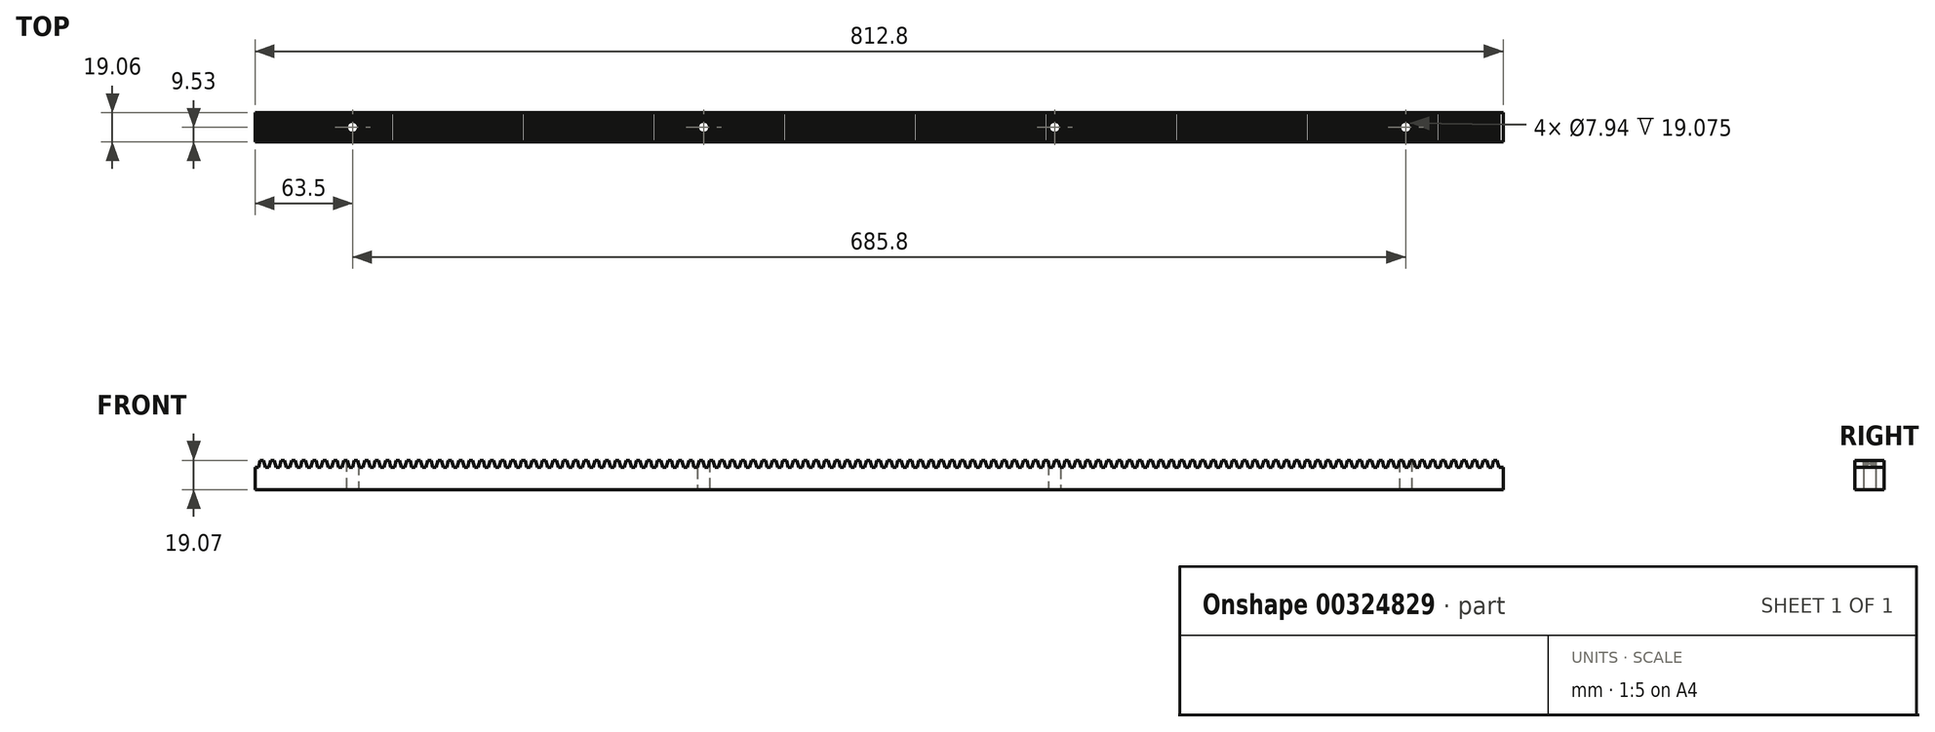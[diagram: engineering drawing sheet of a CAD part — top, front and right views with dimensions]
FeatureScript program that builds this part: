
annotation { "Feature Type Name" : "Feature", "Feature Type Description" : "" }
export const myFeature = defineFeature(function(context is Context, id is Id, definition is map)
    precondition{}
    {
        {
            var Q0;
            Q0=qCreatedBy(makeId("Right.planeOp"),FACE);
            var sketch = newSketch(context, id + "F0", { "sketchPlane" : qUnion([Q0])});
            skLineSegment(sketch, "E0.bottom", {"start": v(-9.52, 7.25) * mm, "end": v(9.53, 7.25) * mm});
            skLineSegment(sketch, "E0.top", {"start": v(-9.53, -7.25) * mm, "end": v(9.52, -7.25) * mm});
            skLineSegment(sketch, "E0.left", {"start": v(-9.52, 7.25) * mm, "end": v(-9.53, -7.25) * mm});
            skLineSegment(sketch, "E0.right", {"start": v(9.53, 7.25) * mm, "end": v(9.52, -7.25) * mm});
            skPoint(sketch, "E0.middle", {"position": v(0, 0) * mm});
            skSolve(sketch);
        }
        {
            var Q0;
            Q0=qSketchRegion(id+"F0",true);
            extrude(context, id + "F1", {"entities" : qUnion([Q0]), "endBound" : BoundingType.SYMMETRIC, "depth" : 812.8 * mm});
        }
        {
            var Q0;
            Q0=makeQuery(id+"F1.opExtrude","SWEPT_FACE",FACE,{"disambiguationData":[OSD([sQuery(id+"F0.wireOp",EDGE,"E0.left")])]});
            var sketch = newSketch(context, id + "F2", { "sketchPlane" : qUnion([Q0])});
            skLineSegment(sketch, "E1.0", {"start": v(406.4, 7.25) * mm, "end": v(-406.4, 7.25) * mm});
            skLineSegment(sketch, "E2.0", {"start": v(406.4, 11.82) * mm, "end": v(-406.4, 11.82) * mm, "construction": true});
            skLineSegment(sketch, "E3", {"start": v(-406.4, 7.25) * mm, "end": v(-406.4, 19.13) * mm, "construction": true});
            skLineSegment(sketch, "E4.0", {"start": v(-404.16, 7.25) * mm, "end": v(-404.16, 19.13) * mm, "construction": true});
            skLineSegment(sketch, "E5.0", {"start": v(-403, 7.25) * mm, "end": v(-403, 19.13) * mm, "construction": true});
            skLineSegment(sketch, "E6.0", {"start": v(-400.76, 7.25) * mm, "end": v(-400.76, 19.13) * mm, "construction": true});
            skLineSegment(sketch, "E7.0", {"start": v(-399.6, 7.25) * mm, "end": v(-399.6, 19.13) * mm, "construction": true});
            skLineSegment(sketch, "E8", {"start": v(-406.4, 7.25) * mm, "end": v(-404.16, 7.25) * mm});
            skLineSegment(sketch, "E9", {"start": v(-403, 11.82) * mm, "end": v(-404.16, 7.25) * mm});
            skLineSegment(sketch, "E10", {"start": v(-403, 11.82) * mm, "end": v(-400.76, 11.82) * mm});
            skLineSegment(sketch, "E11", {"start": v(-400.76, 11.82) * mm, "end": v(-399.6, 7.25) * mm});
            skLineSegment(sketch, "E12.1.0.0", {"start": v(-399.6, 7.25) * mm, "end": v(-397.36, 7.25) * mm});
            skLineSegment(sketch, "E12.1.0.1", {"start": v(-393.95, 11.82) * mm, "end": v(-392.79, 7.25) * mm});
            skLineSegment(sketch, "E12.1.0.2", {"start": v(-396.19, 11.82) * mm, "end": v(-393.95, 11.82) * mm});
            skLineSegment(sketch, "E12.1.0.3", {"start": v(-396.19, 11.82) * mm, "end": v(-397.36, 7.25) * mm});
            skLineSegment(sketch, "E12.2.0.0", {"start": v(-392.79, 7.25) * mm, "end": v(-390.55, 7.25) * mm});
            skLineSegment(sketch, "E12.2.0.1", {"start": v(-387.15, 11.82) * mm, "end": v(-385.98, 7.25) * mm});
            skLineSegment(sketch, "E12.2.0.2", {"start": v(-389.38, 11.82) * mm, "end": v(-387.15, 11.82) * mm});
            skLineSegment(sketch, "E12.2.0.3", {"start": v(-389.38, 11.82) * mm, "end": v(-390.55, 7.25) * mm});
            skLineSegment(sketch, "E12.3.0.0", {"start": v(-385.98, 7.25) * mm, "end": v(-383.74, 7.25) * mm});
            skLineSegment(sketch, "E12.3.0.1", {"start": v(-380.34, 11.82) * mm, "end": v(-379.17, 7.25) * mm});
            skLineSegment(sketch, "E12.3.0.2", {"start": v(-382.57, 11.82) * mm, "end": v(-380.34, 11.82) * mm});
            skLineSegment(sketch, "E12.3.0.3", {"start": v(-382.57, 11.82) * mm, "end": v(-383.74, 7.25) * mm});
            skLineSegment(sketch, "E12.4.0.0", {"start": v(-379.17, 7.25) * mm, "end": v(-376.94, 7.25) * mm});
            skLineSegment(sketch, "E12.4.0.1", {"start": v(-373.53, 11.82) * mm, "end": v(-372.36, 7.25) * mm});
            skLineSegment(sketch, "E12.4.0.2", {"start": v(-375.77, 11.82) * mm, "end": v(-373.53, 11.82) * mm});
            skLineSegment(sketch, "E12.4.0.3", {"start": v(-375.77, 11.82) * mm, "end": v(-376.94, 7.25) * mm});
            skLineSegment(sketch, "E12.5.0.0", {"start": v(-372.36, 7.25) * mm, "end": v(-370.13, 7.25) * mm});
            skLineSegment(sketch, "E12.5.0.1", {"start": v(-366.73, 11.82) * mm, "end": v(-365.56, 7.25) * mm});
            skLineSegment(sketch, "E12.5.0.2", {"start": v(-368.96, 11.82) * mm, "end": v(-366.73, 11.82) * mm});
            skLineSegment(sketch, "E12.5.0.3", {"start": v(-368.96, 11.82) * mm, "end": v(-370.13, 7.25) * mm});
            skLineSegment(sketch, "E12.6.0.0", {"start": v(-365.56, 7.25) * mm, "end": v(-363.32, 7.25) * mm});
            skLineSegment(sketch, "E12.6.0.1", {"start": v(-359.92, 11.82) * mm, "end": v(-358.75, 7.25) * mm});
            skLineSegment(sketch, "E12.6.0.2", {"start": v(-362.15, 11.82) * mm, "end": v(-359.92, 11.82) * mm});
            skLineSegment(sketch, "E12.6.0.3", {"start": v(-362.15, 11.82) * mm, "end": v(-363.32, 7.25) * mm});
            skLineSegment(sketch, "E12.7.0.0", {"start": v(-358.75, 7.25) * mm, "end": v(-356.51, 7.25) * mm});
            skLineSegment(sketch, "E12.7.0.1", {"start": v(-353.11, 11.82) * mm, "end": v(-351.94, 7.25) * mm});
            skLineSegment(sketch, "E12.7.0.2", {"start": v(-355.35, 11.82) * mm, "end": v(-353.11, 11.82) * mm});
            skLineSegment(sketch, "E12.7.0.3", {"start": v(-355.35, 11.82) * mm, "end": v(-356.51, 7.25) * mm});
            skLineSegment(sketch, "E12.8.0.0", {"start": v(-351.94, 7.25) * mm, "end": v(-349.7, 7.25) * mm});
            skLineSegment(sketch, "E12.8.0.1", {"start": v(-346.3, 11.82) * mm, "end": v(-345.14, 7.25) * mm});
            skLineSegment(sketch, "E12.8.0.2", {"start": v(-348.54, 11.82) * mm, "end": v(-346.3, 11.82) * mm});
            skLineSegment(sketch, "E12.8.0.3", {"start": v(-348.54, 11.82) * mm, "end": v(-349.7, 7.25) * mm});
            skLineSegment(sketch, "E12.9.0.0", {"start": v(-345.14, 7.25) * mm, "end": v(-342.9, 7.25) * mm});
            skLineSegment(sketch, "E12.9.0.1", {"start": v(-339.5, 11.82) * mm, "end": v(-338.33, 7.25) * mm});
            skLineSegment(sketch, "E12.9.0.2", {"start": v(-341.73, 11.82) * mm, "end": v(-339.5, 11.82) * mm});
            skLineSegment(sketch, "E12.9.0.3", {"start": v(-341.73, 11.82) * mm, "end": v(-342.9, 7.25) * mm});
            skLineSegment(sketch, "E12.10.0.0", {"start": v(-338.33, 7.25) * mm, "end": v(-336.1, 7.25) * mm});
            skLineSegment(sketch, "E12.10.0.1", {"start": v(-332.69, 11.82) * mm, "end": v(-331.52, 7.25) * mm});
            skLineSegment(sketch, "E12.10.0.2", {"start": v(-334.92, 11.82) * mm, "end": v(-332.69, 11.82) * mm});
            skLineSegment(sketch, "E12.10.0.3", {"start": v(-334.92, 11.82) * mm, "end": v(-336.1, 7.25) * mm});
            skLineSegment(sketch, "E12.11.0.0", {"start": v(-331.52, 7.25) * mm, "end": v(-329.29, 7.25) * mm});
            skLineSegment(sketch, "E12.11.0.1", {"start": v(-325.88, 11.82) * mm, "end": v(-324.71, 7.25) * mm});
            skLineSegment(sketch, "E12.11.0.2", {"start": v(-328.12, 11.82) * mm, "end": v(-325.88, 11.82) * mm});
            skLineSegment(sketch, "E12.11.0.3", {"start": v(-328.12, 11.82) * mm, "end": v(-329.29, 7.25) * mm});
            skLineSegment(sketch, "E12.12.0.0", {"start": v(-324.71, 7.25) * mm, "end": v(-322.48, 7.25) * mm});
            skLineSegment(sketch, "E12.12.0.1", {"start": v(-319.07, 11.82) * mm, "end": v(-317.9, 7.25) * mm});
            skLineSegment(sketch, "E12.12.0.2", {"start": v(-321.3, 11.82) * mm, "end": v(-319.07, 11.82) * mm});
            skLineSegment(sketch, "E12.12.0.3", {"start": v(-321.3, 11.82) * mm, "end": v(-322.48, 7.25) * mm});
            skLineSegment(sketch, "E12.13.0.0", {"start": v(-317.9, 7.25) * mm, "end": v(-315.67, 7.25) * mm});
            skLineSegment(sketch, "E12.13.0.1", {"start": v(-312.27, 11.82) * mm, "end": v(-311.1, 7.25) * mm});
            skLineSegment(sketch, "E12.13.0.2", {"start": v(-314.5, 11.82) * mm, "end": v(-312.27, 11.82) * mm});
            skLineSegment(sketch, "E12.13.0.3", {"start": v(-314.5, 11.82) * mm, "end": v(-315.67, 7.25) * mm});
            skLineSegment(sketch, "E12.14.0.0", {"start": v(-311.1, 7.25) * mm, "end": v(-308.86, 7.25) * mm});
            skLineSegment(sketch, "E12.14.0.1", {"start": v(-305.46, 11.82) * mm, "end": v(-304.3, 7.25) * mm});
            skLineSegment(sketch, "E12.14.0.2", {"start": v(-307.7, 11.82) * mm, "end": v(-305.46, 11.82) * mm});
            skLineSegment(sketch, "E12.14.0.3", {"start": v(-307.7, 11.82) * mm, "end": v(-308.86, 7.25) * mm});
            skLineSegment(sketch, "E12.15.0.0", {"start": v(-304.3, 7.25) * mm, "end": v(-302.06, 7.25) * mm});
            skLineSegment(sketch, "E12.15.0.1", {"start": v(-298.65, 11.82) * mm, "end": v(-297.48, 7.25) * mm});
            skLineSegment(sketch, "E12.15.0.2", {"start": v(-300.89, 11.82) * mm, "end": v(-298.65, 11.82) * mm});
            skLineSegment(sketch, "E12.15.0.3", {"start": v(-300.89, 11.82) * mm, "end": v(-302.06, 7.25) * mm});
            skLineSegment(sketch, "E12.16.0.0", {"start": v(-297.48, 7.25) * mm, "end": v(-295.25, 7.25) * mm});
            skLineSegment(sketch, "E12.16.0.1", {"start": v(-291.85, 11.82) * mm, "end": v(-290.68, 7.25) * mm});
            skLineSegment(sketch, "E12.16.0.2", {"start": v(-294.08, 11.82) * mm, "end": v(-291.85, 11.82) * mm});
            skLineSegment(sketch, "E12.16.0.3", {"start": v(-294.08, 11.82) * mm, "end": v(-295.25, 7.25) * mm});
            skLineSegment(sketch, "E12.17.0.0", {"start": v(-290.68, 7.25) * mm, "end": v(-288.44, 7.25) * mm});
            skLineSegment(sketch, "E12.17.0.1", {"start": v(-285.04, 11.82) * mm, "end": v(-283.87, 7.25) * mm});
            skLineSegment(sketch, "E12.17.0.2", {"start": v(-287.27, 11.82) * mm, "end": v(-285.04, 11.82) * mm});
            skLineSegment(sketch, "E12.17.0.3", {"start": v(-287.27, 11.82) * mm, "end": v(-288.44, 7.25) * mm});
            skLineSegment(sketch, "E12.18.0.0", {"start": v(-283.87, 7.25) * mm, "end": v(-281.64, 7.25) * mm});
            skLineSegment(sketch, "E12.18.0.1", {"start": v(-278.23, 11.82) * mm, "end": v(-277.06, 7.25) * mm});
            skLineSegment(sketch, "E12.18.0.2", {"start": v(-280.47, 11.82) * mm, "end": v(-278.23, 11.82) * mm});
            skLineSegment(sketch, "E12.18.0.3", {"start": v(-280.47, 11.82) * mm, "end": v(-281.64, 7.25) * mm});
            skLineSegment(sketch, "E12.19.0.0", {"start": v(-277.06, 7.25) * mm, "end": v(-274.83, 7.25) * mm});
            skLineSegment(sketch, "E12.19.0.1", {"start": v(-271.42, 11.82) * mm, "end": v(-270.26, 7.25) * mm});
            skLineSegment(sketch, "E12.19.0.2", {"start": v(-273.66, 11.82) * mm, "end": v(-271.42, 11.82) * mm});
            skLineSegment(sketch, "E12.19.0.3", {"start": v(-273.66, 11.82) * mm, "end": v(-274.83, 7.25) * mm});
            skLineSegment(sketch, "E12.direction1", {"start": v(-406.4, 7.25) * mm, "end": v(-399.6, 7.25) * mm, "construction": true});
            skLineSegment(sketch, "E13.1.0.0", {"start": v(-264.62, 11.82) * mm, "end": v(-263.45, 7.25) * mm});
            skLineSegment(sketch, "E13.1.0.1", {"start": v(-266.85, 11.82) * mm, "end": v(-264.62, 11.82) * mm});
            skLineSegment(sketch, "E13.1.0.2", {"start": v(-266.85, 11.82) * mm, "end": v(-268.02, 7.25) * mm});
            skLineSegment(sketch, "E13.1.0.3", {"start": v(-270.26, 7.25) * mm, "end": v(-268.02, 7.25) * mm});
            skLineSegment(sketch, "E13.2.0.0", {"start": v(-257.8, 11.82) * mm, "end": v(-256.64, 7.25) * mm});
            skLineSegment(sketch, "E13.2.0.1", {"start": v(-260.05, 11.82) * mm, "end": v(-257.8, 11.82) * mm});
            skLineSegment(sketch, "E13.2.0.2", {"start": v(-260.05, 11.82) * mm, "end": v(-261.21, 7.25) * mm});
            skLineSegment(sketch, "E13.2.0.3", {"start": v(-263.45, 7.25) * mm, "end": v(-261.21, 7.25) * mm});
            skLineSegment(sketch, "E13.3.0.0", {"start": v(-251, 11.82) * mm, "end": v(-249.83, 7.25) * mm});
            skLineSegment(sketch, "E13.3.0.1", {"start": v(-253.24, 11.82) * mm, "end": v(-251, 11.82) * mm});
            skLineSegment(sketch, "E13.3.0.2", {"start": v(-253.24, 11.82) * mm, "end": v(-254.4, 7.25) * mm});
            skLineSegment(sketch, "E13.3.0.3", {"start": v(-256.64, 7.25) * mm, "end": v(-254.4, 7.25) * mm});
            skLineSegment(sketch, "E13.4.0.0", {"start": v(-244.2, 11.82) * mm, "end": v(-243.03, 7.25) * mm});
            skLineSegment(sketch, "E13.4.0.1", {"start": v(-246.43, 11.82) * mm, "end": v(-244.2, 11.82) * mm});
            skLineSegment(sketch, "E13.4.0.2", {"start": v(-246.43, 11.82) * mm, "end": v(-247.6, 7.25) * mm});
            skLineSegment(sketch, "E13.4.0.3", {"start": v(-249.83, 7.25) * mm, "end": v(-247.6, 7.25) * mm});
            skLineSegment(sketch, "E13.5.0.0", {"start": v(-237.39, 11.82) * mm, "end": v(-236.22, 7.25) * mm});
            skLineSegment(sketch, "E13.5.0.1", {"start": v(-239.62, 11.82) * mm, "end": v(-237.39, 11.82) * mm});
            skLineSegment(sketch, "E13.5.0.2", {"start": v(-239.62, 11.82) * mm, "end": v(-240.8, 7.25) * mm});
            skLineSegment(sketch, "E13.5.0.3", {"start": v(-243.03, 7.25) * mm, "end": v(-240.8, 7.25) * mm});
            skLineSegment(sketch, "E13.6.0.0", {"start": v(-230.58, 11.82) * mm, "end": v(-229.41, 7.25) * mm});
            skLineSegment(sketch, "E13.6.0.1", {"start": v(-232.82, 11.82) * mm, "end": v(-230.58, 11.82) * mm});
            skLineSegment(sketch, "E13.6.0.2", {"start": v(-232.82, 11.82) * mm, "end": v(-233.98, 7.25) * mm});
            skLineSegment(sketch, "E13.6.0.3", {"start": v(-236.22, 7.25) * mm, "end": v(-233.98, 7.25) * mm});
            skLineSegment(sketch, "E13.7.0.0", {"start": v(-223.77, 11.82) * mm, "end": v(-222.6, 7.25) * mm});
            skLineSegment(sketch, "E13.7.0.1", {"start": v(-226, 11.82) * mm, "end": v(-223.77, 11.82) * mm});
            skLineSegment(sketch, "E13.7.0.2", {"start": v(-226, 11.82) * mm, "end": v(-227.18, 7.25) * mm});
            skLineSegment(sketch, "E13.7.0.3", {"start": v(-229.41, 7.25) * mm, "end": v(-227.18, 7.25) * mm});
            skLineSegment(sketch, "E13.8.0.0", {"start": v(-216.97, 11.82) * mm, "end": v(-215.8, 7.25) * mm});
            skLineSegment(sketch, "E13.8.0.1", {"start": v(-219.2, 11.82) * mm, "end": v(-216.97, 11.82) * mm});
            skLineSegment(sketch, "E13.8.0.2", {"start": v(-219.2, 11.82) * mm, "end": v(-220.37, 7.25) * mm});
            skLineSegment(sketch, "E13.8.0.3", {"start": v(-222.6, 7.25) * mm, "end": v(-220.37, 7.25) * mm});
            skLineSegment(sketch, "E13.9.0.0", {"start": v(-210.16, 11.82) * mm, "end": v(-209, 7.25) * mm});
            skLineSegment(sketch, "E13.9.0.1", {"start": v(-212.4, 11.82) * mm, "end": v(-210.16, 11.82) * mm});
            skLineSegment(sketch, "E13.9.0.2", {"start": v(-212.4, 11.82) * mm, "end": v(-213.56, 7.25) * mm});
            skLineSegment(sketch, "E13.9.0.3", {"start": v(-215.8, 7.25) * mm, "end": v(-213.56, 7.25) * mm});
            skLineSegment(sketch, "E13.10.0.0", {"start": v(-203.35, 11.82) * mm, "end": v(-202.18, 7.25) * mm});
            skLineSegment(sketch, "E13.10.0.1", {"start": v(-205.59, 11.82) * mm, "end": v(-203.35, 11.82) * mm});
            skLineSegment(sketch, "E13.10.0.2", {"start": v(-205.59, 11.82) * mm, "end": v(-206.76, 7.25) * mm});
            skLineSegment(sketch, "E13.10.0.3", {"start": v(-209, 7.25) * mm, "end": v(-206.76, 7.25) * mm});
            skLineSegment(sketch, "E13.11.0.0", {"start": v(-196.55, 11.82) * mm, "end": v(-195.38, 7.25) * mm});
            skLineSegment(sketch, "E13.11.0.1", {"start": v(-198.78, 11.82) * mm, "end": v(-196.55, 11.82) * mm});
            skLineSegment(sketch, "E13.11.0.2", {"start": v(-198.78, 11.82) * mm, "end": v(-199.95, 7.25) * mm});
            skLineSegment(sketch, "E13.11.0.3", {"start": v(-202.18, 7.25) * mm, "end": v(-199.95, 7.25) * mm});
            skLineSegment(sketch, "E13.12.0.0", {"start": v(-189.74, 11.82) * mm, "end": v(-188.57, 7.25) * mm});
            skLineSegment(sketch, "E13.12.0.1", {"start": v(-191.97, 11.82) * mm, "end": v(-189.74, 11.82) * mm});
            skLineSegment(sketch, "E13.12.0.2", {"start": v(-191.97, 11.82) * mm, "end": v(-193.14, 7.25) * mm});
            skLineSegment(sketch, "E13.12.0.3", {"start": v(-195.38, 7.25) * mm, "end": v(-193.14, 7.25) * mm});
            skLineSegment(sketch, "E13.13.0.0", {"start": v(-182.93, 11.82) * mm, "end": v(-181.76, 7.25) * mm});
            skLineSegment(sketch, "E13.13.0.1", {"start": v(-185.17, 11.82) * mm, "end": v(-182.93, 11.82) * mm});
            skLineSegment(sketch, "E13.13.0.2", {"start": v(-185.17, 11.82) * mm, "end": v(-186.33, 7.25) * mm});
            skLineSegment(sketch, "E13.13.0.3", {"start": v(-188.57, 7.25) * mm, "end": v(-186.33, 7.25) * mm});
            skLineSegment(sketch, "E13.14.0.0", {"start": v(-176.12, 11.82) * mm, "end": v(-174.96, 7.25) * mm});
            skLineSegment(sketch, "E13.14.0.1", {"start": v(-178.36, 11.82) * mm, "end": v(-176.12, 11.82) * mm});
            skLineSegment(sketch, "E13.14.0.2", {"start": v(-178.36, 11.82) * mm, "end": v(-179.53, 7.25) * mm});
            skLineSegment(sketch, "E13.14.0.3", {"start": v(-181.76, 7.25) * mm, "end": v(-179.53, 7.25) * mm});
            skLineSegment(sketch, "E13.15.0.0", {"start": v(-169.32, 11.82) * mm, "end": v(-168.15, 7.25) * mm});
            skLineSegment(sketch, "E13.15.0.1", {"start": v(-171.55, 11.82) * mm, "end": v(-169.32, 11.82) * mm});
            skLineSegment(sketch, "E13.15.0.2", {"start": v(-171.55, 11.82) * mm, "end": v(-172.72, 7.25) * mm});
            skLineSegment(sketch, "E13.15.0.3", {"start": v(-174.96, 7.25) * mm, "end": v(-172.72, 7.25) * mm});
            skLineSegment(sketch, "E13.16.0.0", {"start": v(-162.5, 11.82) * mm, "end": v(-161.34, 7.25) * mm});
            skLineSegment(sketch, "E13.16.0.1", {"start": v(-164.74, 11.82) * mm, "end": v(-162.5, 11.82) * mm});
            skLineSegment(sketch, "E13.16.0.2", {"start": v(-164.74, 11.82) * mm, "end": v(-165.91, 7.25) * mm});
            skLineSegment(sketch, "E13.16.0.3", {"start": v(-168.15, 7.25) * mm, "end": v(-165.91, 7.25) * mm});
            skLineSegment(sketch, "E13.17.0.0", {"start": v(-155.7, 11.82) * mm, "end": v(-154.53, 7.25) * mm});
            skLineSegment(sketch, "E13.17.0.1", {"start": v(-157.94, 11.82) * mm, "end": v(-155.7, 11.82) * mm});
            skLineSegment(sketch, "E13.17.0.2", {"start": v(-157.94, 11.82) * mm, "end": v(-159.1, 7.25) * mm});
            skLineSegment(sketch, "E13.17.0.3", {"start": v(-161.34, 7.25) * mm, "end": v(-159.1, 7.25) * mm});
            skLineSegment(sketch, "E13.18.0.0", {"start": v(-148.9, 11.82) * mm, "end": v(-147.73, 7.25) * mm});
            skLineSegment(sketch, "E13.18.0.1", {"start": v(-151.13, 11.82) * mm, "end": v(-148.9, 11.82) * mm});
            skLineSegment(sketch, "E13.18.0.2", {"start": v(-151.13, 11.82) * mm, "end": v(-152.3, 7.25) * mm});
            skLineSegment(sketch, "E13.18.0.3", {"start": v(-154.53, 7.25) * mm, "end": v(-152.3, 7.25) * mm});
            skLineSegment(sketch, "E13.19.0.0", {"start": v(-142.09, 11.82) * mm, "end": v(-140.92, 7.25) * mm});
            skLineSegment(sketch, "E13.19.0.1", {"start": v(-144.32, 11.82) * mm, "end": v(-142.09, 11.82) * mm});
            skLineSegment(sketch, "E13.19.0.2", {"start": v(-144.32, 11.82) * mm, "end": v(-145.5, 7.25) * mm});
            skLineSegment(sketch, "E13.19.0.3", {"start": v(-147.73, 7.25) * mm, "end": v(-145.5, 7.25) * mm});
            skLineSegment(sketch, "E13.direction1", {"start": v(-277.06, 7.25) * mm, "end": v(-270.26, 7.25) * mm, "construction": true});
            skLineSegment(sketch, "E14.1.0.0", {"start": v(-140.92, 7.25) * mm, "end": v(-138.68, 7.25) * mm});
            skLineSegment(sketch, "E14.1.0.1", {"start": v(-135.28, 11.82) * mm, "end": v(-134.11, 7.25) * mm});
            skLineSegment(sketch, "E14.1.0.2", {"start": v(-137.52, 11.82) * mm, "end": v(-138.68, 7.25) * mm});
            skLineSegment(sketch, "E14.1.0.3", {"start": v(-137.52, 11.82) * mm, "end": v(-135.28, 11.82) * mm});
            skLineSegment(sketch, "E14.2.0.0", {"start": v(-134.11, 7.25) * mm, "end": v(-131.88, 7.25) * mm});
            skLineSegment(sketch, "E14.2.0.1", {"start": v(-128.47, 11.82) * mm, "end": v(-127.3, 7.25) * mm});
            skLineSegment(sketch, "E14.2.0.2", {"start": v(-130.7, 11.82) * mm, "end": v(-131.88, 7.25) * mm});
            skLineSegment(sketch, "E14.2.0.3", {"start": v(-130.7, 11.82) * mm, "end": v(-128.47, 11.82) * mm});
            skLineSegment(sketch, "E14.3.0.0", {"start": v(-127.3, 7.25) * mm, "end": v(-125.07, 7.25) * mm});
            skLineSegment(sketch, "E14.3.0.1", {"start": v(-121.67, 11.82) * mm, "end": v(-120.5, 7.25) * mm});
            skLineSegment(sketch, "E14.3.0.2", {"start": v(-123.9, 11.82) * mm, "end": v(-125.07, 7.25) * mm});
            skLineSegment(sketch, "E14.3.0.3", {"start": v(-123.9, 11.82) * mm, "end": v(-121.67, 11.82) * mm});
            skLineSegment(sketch, "E14.4.0.0", {"start": v(-120.5, 7.25) * mm, "end": v(-118.26, 7.25) * mm});
            skLineSegment(sketch, "E14.4.0.1", {"start": v(-114.86, 11.82) * mm, "end": v(-113.7, 7.25) * mm});
            skLineSegment(sketch, "E14.4.0.2", {"start": v(-117.1, 11.82) * mm, "end": v(-118.26, 7.25) * mm});
            skLineSegment(sketch, "E14.4.0.3", {"start": v(-117.1, 11.82) * mm, "end": v(-114.86, 11.82) * mm});
            skLineSegment(sketch, "E14.5.0.0", {"start": v(-113.7, 7.25) * mm, "end": v(-111.46, 7.25) * mm});
            skLineSegment(sketch, "E14.5.0.1", {"start": v(-108.05, 11.82) * mm, "end": v(-106.88, 7.25) * mm});
            skLineSegment(sketch, "E14.5.0.2", {"start": v(-110.29, 11.82) * mm, "end": v(-111.46, 7.25) * mm});
            skLineSegment(sketch, "E14.5.0.3", {"start": v(-110.29, 11.82) * mm, "end": v(-108.05, 11.82) * mm});
            skLineSegment(sketch, "E14.6.0.0", {"start": v(-106.88, 7.25) * mm, "end": v(-104.65, 7.25) * mm});
            skLineSegment(sketch, "E14.6.0.1", {"start": v(-101.24, 11.82) * mm, "end": v(-100.08, 7.25) * mm});
            skLineSegment(sketch, "E14.6.0.2", {"start": v(-103.48, 11.82) * mm, "end": v(-104.65, 7.25) * mm});
            skLineSegment(sketch, "E14.6.0.3", {"start": v(-103.48, 11.82) * mm, "end": v(-101.24, 11.82) * mm});
            skLineSegment(sketch, "E14.7.0.0", {"start": v(-100.08, 7.25) * mm, "end": v(-97.84, 7.25) * mm});
            skLineSegment(sketch, "E14.7.0.1", {"start": v(-94.44, 11.82) * mm, "end": v(-93.27, 7.25) * mm});
            skLineSegment(sketch, "E14.7.0.2", {"start": v(-96.67, 11.82) * mm, "end": v(-97.84, 7.25) * mm});
            skLineSegment(sketch, "E14.7.0.3", {"start": v(-96.67, 11.82) * mm, "end": v(-94.44, 11.82) * mm});
            skLineSegment(sketch, "E14.8.0.0", {"start": v(-93.27, 7.25) * mm, "end": v(-91.03, 7.25) * mm});
            skLineSegment(sketch, "E14.8.0.1", {"start": v(-87.63, 11.82) * mm, "end": v(-86.46, 7.25) * mm});
            skLineSegment(sketch, "E14.8.0.2", {"start": v(-89.87, 11.82) * mm, "end": v(-91.03, 7.25) * mm});
            skLineSegment(sketch, "E14.8.0.3", {"start": v(-89.87, 11.82) * mm, "end": v(-87.63, 11.82) * mm});
            skLineSegment(sketch, "E14.9.0.0", {"start": v(-86.46, 7.25) * mm, "end": v(-84.23, 7.25) * mm});
            skLineSegment(sketch, "E14.9.0.1", {"start": v(-80.82, 11.82) * mm, "end": v(-79.65, 7.25) * mm});
            skLineSegment(sketch, "E14.9.0.2", {"start": v(-83.06, 11.82) * mm, "end": v(-84.23, 7.25) * mm});
            skLineSegment(sketch, "E14.9.0.3", {"start": v(-83.06, 11.82) * mm, "end": v(-80.82, 11.82) * mm});
            skLineSegment(sketch, "E14.10.0.0", {"start": v(-79.65, 7.25) * mm, "end": v(-77.42, 7.25) * mm});
            skLineSegment(sketch, "E14.10.0.1", {"start": v(-74.02, 11.82) * mm, "end": v(-72.85, 7.25) * mm});
            skLineSegment(sketch, "E14.10.0.2", {"start": v(-76.25, 11.82) * mm, "end": v(-77.42, 7.25) * mm});
            skLineSegment(sketch, "E14.10.0.3", {"start": v(-76.25, 11.82) * mm, "end": v(-74.02, 11.82) * mm});
            skLineSegment(sketch, "E14.11.0.0", {"start": v(-72.85, 7.25) * mm, "end": v(-70.61, 7.25) * mm});
            skLineSegment(sketch, "E14.11.0.1", {"start": v(-67.2, 11.82) * mm, "end": v(-66.04, 7.25) * mm});
            skLineSegment(sketch, "E14.11.0.2", {"start": v(-69.44, 11.82) * mm, "end": v(-70.61, 7.25) * mm});
            skLineSegment(sketch, "E14.11.0.3", {"start": v(-69.44, 11.82) * mm, "end": v(-67.2, 11.82) * mm});
            skLineSegment(sketch, "E14.12.0.0", {"start": v(-66.04, 7.25) * mm, "end": v(-63.8, 7.25) * mm});
            skLineSegment(sketch, "E14.12.0.1", {"start": v(-60.4, 11.82) * mm, "end": v(-59.23, 7.25) * mm});
            skLineSegment(sketch, "E14.12.0.2", {"start": v(-62.64, 11.82) * mm, "end": v(-63.8, 7.25) * mm});
            skLineSegment(sketch, "E14.12.0.3", {"start": v(-62.64, 11.82) * mm, "end": v(-60.4, 11.82) * mm});
            skLineSegment(sketch, "E14.13.0.0", {"start": v(-59.23, 7.25) * mm, "end": v(-57, 7.25) * mm});
            skLineSegment(sketch, "E14.13.0.1", {"start": v(-53.6, 11.82) * mm, "end": v(-52.43, 7.25) * mm});
            skLineSegment(sketch, "E14.13.0.2", {"start": v(-55.83, 11.82) * mm, "end": v(-57, 7.25) * mm});
            skLineSegment(sketch, "E14.13.0.3", {"start": v(-55.83, 11.82) * mm, "end": v(-53.6, 11.82) * mm});
            skLineSegment(sketch, "E14.14.0.0", {"start": v(-52.43, 7.25) * mm, "end": v(-50.2, 7.25) * mm});
            skLineSegment(sketch, "E14.14.0.1", {"start": v(-46.79, 11.82) * mm, "end": v(-45.62, 7.25) * mm});
            skLineSegment(sketch, "E14.14.0.2", {"start": v(-49.02, 11.82) * mm, "end": v(-50.2, 7.25) * mm});
            skLineSegment(sketch, "E14.14.0.3", {"start": v(-49.02, 11.82) * mm, "end": v(-46.79, 11.82) * mm});
            skLineSegment(sketch, "E14.15.0.0", {"start": v(-45.62, 7.25) * mm, "end": v(-43.38, 7.25) * mm});
            skLineSegment(sketch, "E14.15.0.1", {"start": v(-39.98, 11.82) * mm, "end": v(-38.81, 7.25) * mm});
            skLineSegment(sketch, "E14.15.0.2", {"start": v(-42.21, 11.82) * mm, "end": v(-43.38, 7.25) * mm});
            skLineSegment(sketch, "E14.15.0.3", {"start": v(-42.21, 11.82) * mm, "end": v(-39.98, 11.82) * mm});
            skLineSegment(sketch, "E14.16.0.0", {"start": v(-38.81, 7.25) * mm, "end": v(-36.58, 7.25) * mm});
            skLineSegment(sketch, "E14.16.0.1", {"start": v(-33.17, 11.82) * mm, "end": v(-32, 7.25) * mm});
            skLineSegment(sketch, "E14.16.0.2", {"start": v(-35.4, 11.82) * mm, "end": v(-36.58, 7.25) * mm});
            skLineSegment(sketch, "E14.16.0.3", {"start": v(-35.4, 11.82) * mm, "end": v(-33.17, 11.82) * mm});
            skLineSegment(sketch, "E14.17.0.0", {"start": v(-32, 7.25) * mm, "end": v(-29.77, 7.25) * mm});
            skLineSegment(sketch, "E14.17.0.1", {"start": v(-26.37, 11.82) * mm, "end": v(-25.2, 7.25) * mm});
            skLineSegment(sketch, "E14.17.0.2", {"start": v(-28.6, 11.82) * mm, "end": v(-29.77, 7.25) * mm});
            skLineSegment(sketch, "E14.17.0.3", {"start": v(-28.6, 11.82) * mm, "end": v(-26.37, 11.82) * mm});
            skLineSegment(sketch, "E14.18.0.0", {"start": v(-25.2, 7.25) * mm, "end": v(-22.96, 7.25) * mm});
            skLineSegment(sketch, "E14.18.0.1", {"start": v(-19.56, 11.82) * mm, "end": v(-18.39, 7.25) * mm});
            skLineSegment(sketch, "E14.18.0.2", {"start": v(-21.8, 11.82) * mm, "end": v(-22.96, 7.25) * mm});
            skLineSegment(sketch, "E14.18.0.3", {"start": v(-21.8, 11.82) * mm, "end": v(-19.56, 11.82) * mm});
            skLineSegment(sketch, "E14.19.0.0", {"start": v(-18.39, 7.25) * mm, "end": v(-16.15, 7.25) * mm});
            skLineSegment(sketch, "E14.19.0.1", {"start": v(-12.75, 11.82) * mm, "end": v(-11.58, 7.25) * mm});
            skLineSegment(sketch, "E14.19.0.2", {"start": v(-14.99, 11.82) * mm, "end": v(-16.15, 7.25) * mm});
            skLineSegment(sketch, "E14.19.0.3", {"start": v(-14.99, 11.82) * mm, "end": v(-12.75, 11.82) * mm});
            skLineSegment(sketch, "E14.20.0.0", {"start": v(-11.58, 7.25) * mm, "end": v(-9.35, 7.25) * mm});
            skLineSegment(sketch, "E14.20.0.1", {"start": v(-5.94, 11.82) * mm, "end": v(-4.78, 7.25) * mm});
            skLineSegment(sketch, "E14.20.0.2", {"start": v(-8.18, 11.82) * mm, "end": v(-9.35, 7.25) * mm});
            skLineSegment(sketch, "E14.20.0.3", {"start": v(-8.18, 11.82) * mm, "end": v(-5.94, 11.82) * mm});
            skLineSegment(sketch, "E14.21.0.0", {"start": v(-4.78, 7.25) * mm, "end": v(-2.54, 7.25) * mm});
            skLineSegment(sketch, "E14.21.0.1", {"start": v(0.86, 11.82) * mm, "end": v(2.03, 7.25) * mm});
            skLineSegment(sketch, "E14.21.0.2", {"start": v(-1.37, 11.82) * mm, "end": v(-2.54, 7.25) * mm});
            skLineSegment(sketch, "E14.21.0.3", {"start": v(-1.37, 11.82) * mm, "end": v(0.86, 11.82) * mm});
            skLineSegment(sketch, "E14.22.0.0", {"start": v(2.03, 7.25) * mm, "end": v(4.27, 7.25) * mm});
            skLineSegment(sketch, "E14.22.0.1", {"start": v(7.67, 11.82) * mm, "end": v(8.84, 7.25) * mm});
            skLineSegment(sketch, "E14.22.0.2", {"start": v(5.44, 11.82) * mm, "end": v(4.27, 7.25) * mm});
            skLineSegment(sketch, "E14.22.0.3", {"start": v(5.44, 11.82) * mm, "end": v(7.67, 11.82) * mm});
            skLineSegment(sketch, "E14.23.0.0", {"start": v(8.84, 7.25) * mm, "end": v(11.07, 7.25) * mm});
            skLineSegment(sketch, "E14.23.0.1", {"start": v(14.48, 11.82) * mm, "end": v(15.65, 7.25) * mm});
            skLineSegment(sketch, "E14.23.0.2", {"start": v(12.24, 11.82) * mm, "end": v(11.07, 7.25) * mm});
            skLineSegment(sketch, "E14.23.0.3", {"start": v(12.24, 11.82) * mm, "end": v(14.48, 11.82) * mm});
            skLineSegment(sketch, "E14.24.0.0", {"start": v(15.65, 7.25) * mm, "end": v(17.88, 7.25) * mm});
            skLineSegment(sketch, "E14.24.0.1", {"start": v(21.29, 11.82) * mm, "end": v(22.45, 7.25) * mm});
            skLineSegment(sketch, "E14.24.0.2", {"start": v(19.05, 11.82) * mm, "end": v(17.88, 7.25) * mm});
            skLineSegment(sketch, "E14.24.0.3", {"start": v(19.05, 11.82) * mm, "end": v(21.29, 11.82) * mm});
            skLineSegment(sketch, "E14.25.0.0", {"start": v(22.45, 7.25) * mm, "end": v(24.69, 7.25) * mm});
            skLineSegment(sketch, "E14.25.0.1", {"start": v(28.1, 11.82) * mm, "end": v(29.26, 7.25) * mm});
            skLineSegment(sketch, "E14.25.0.2", {"start": v(25.86, 11.82) * mm, "end": v(24.69, 7.25) * mm});
            skLineSegment(sketch, "E14.25.0.3", {"start": v(25.86, 11.82) * mm, "end": v(28.1, 11.82) * mm});
            skLineSegment(sketch, "E14.26.0.0", {"start": v(29.26, 7.25) * mm, "end": v(31.5, 7.25) * mm});
            skLineSegment(sketch, "E14.26.0.1", {"start": v(34.9, 11.82) * mm, "end": v(36.07, 7.25) * mm});
            skLineSegment(sketch, "E14.26.0.2", {"start": v(32.66, 11.82) * mm, "end": v(31.5, 7.25) * mm});
            skLineSegment(sketch, "E14.26.0.3", {"start": v(32.66, 11.82) * mm, "end": v(34.9, 11.82) * mm});
            skLineSegment(sketch, "E14.27.0.0", {"start": v(36.07, 7.25) * mm, "end": v(38.3, 7.25) * mm});
            skLineSegment(sketch, "E14.27.0.1", {"start": v(41.7, 11.82) * mm, "end": v(42.88, 7.25) * mm});
            skLineSegment(sketch, "E14.27.0.2", {"start": v(39.47, 11.82) * mm, "end": v(38.3, 7.25) * mm});
            skLineSegment(sketch, "E14.27.0.3", {"start": v(39.47, 11.82) * mm, "end": v(41.7, 11.82) * mm});
            skLineSegment(sketch, "E14.28.0.0", {"start": v(42.88, 7.25) * mm, "end": v(45.11, 7.25) * mm});
            skLineSegment(sketch, "E14.28.0.1", {"start": v(48.51, 11.82) * mm, "end": v(49.68, 7.25) * mm});
            skLineSegment(sketch, "E14.28.0.2", {"start": v(46.28, 11.82) * mm, "end": v(45.11, 7.25) * mm});
            skLineSegment(sketch, "E14.28.0.3", {"start": v(46.28, 11.82) * mm, "end": v(48.51, 11.82) * mm});
            skLineSegment(sketch, "E14.29.0.0", {"start": v(49.68, 7.25) * mm, "end": v(51.92, 7.25) * mm});
            skLineSegment(sketch, "E14.29.0.1", {"start": v(55.32, 11.82) * mm, "end": v(56.49, 7.25) * mm});
            skLineSegment(sketch, "E14.29.0.2", {"start": v(53.09, 11.82) * mm, "end": v(51.92, 7.25) * mm});
            skLineSegment(sketch, "E14.29.0.3", {"start": v(53.09, 11.82) * mm, "end": v(55.32, 11.82) * mm});
            skLineSegment(sketch, "E14.30.0.0", {"start": v(56.49, 7.25) * mm, "end": v(58.72, 7.25) * mm});
            skLineSegment(sketch, "E14.30.0.1", {"start": v(62.13, 11.82) * mm, "end": v(63.3, 7.25) * mm});
            skLineSegment(sketch, "E14.30.0.2", {"start": v(59.9, 11.82) * mm, "end": v(58.72, 7.25) * mm});
            skLineSegment(sketch, "E14.30.0.3", {"start": v(59.9, 11.82) * mm, "end": v(62.13, 11.82) * mm});
            skLineSegment(sketch, "E14.31.0.0", {"start": v(63.3, 7.25) * mm, "end": v(65.53, 7.25) * mm});
            skLineSegment(sketch, "E14.31.0.1", {"start": v(68.94, 11.82) * mm, "end": v(70.1, 7.25) * mm});
            skLineSegment(sketch, "E14.31.0.2", {"start": v(66.7, 11.82) * mm, "end": v(65.53, 7.25) * mm});
            skLineSegment(sketch, "E14.31.0.3", {"start": v(66.7, 11.82) * mm, "end": v(68.94, 11.82) * mm});
            skLineSegment(sketch, "E14.32.0.0", {"start": v(70.1, 7.25) * mm, "end": v(72.34, 7.25) * mm});
            skLineSegment(sketch, "E14.32.0.1", {"start": v(75.74, 11.82) * mm, "end": v(76.91, 7.25) * mm});
            skLineSegment(sketch, "E14.32.0.2", {"start": v(73.5, 11.82) * mm, "end": v(72.34, 7.25) * mm});
            skLineSegment(sketch, "E14.32.0.3", {"start": v(73.5, 11.82) * mm, "end": v(75.74, 11.82) * mm});
            skLineSegment(sketch, "E14.33.0.0", {"start": v(76.91, 7.25) * mm, "end": v(79.15, 7.25) * mm});
            skLineSegment(sketch, "E14.33.0.1", {"start": v(82.55, 11.82) * mm, "end": v(83.72, 7.25) * mm});
            skLineSegment(sketch, "E14.33.0.2", {"start": v(80.31, 11.82) * mm, "end": v(79.15, 7.25) * mm});
            skLineSegment(sketch, "E14.33.0.3", {"start": v(80.31, 11.82) * mm, "end": v(82.55, 11.82) * mm});
            skLineSegment(sketch, "E14.34.0.0", {"start": v(83.72, 7.25) * mm, "end": v(85.95, 7.25) * mm});
            skLineSegment(sketch, "E14.34.0.1", {"start": v(89.36, 11.82) * mm, "end": v(90.53, 7.25) * mm});
            skLineSegment(sketch, "E14.34.0.2", {"start": v(87.12, 11.82) * mm, "end": v(85.95, 7.25) * mm});
            skLineSegment(sketch, "E14.34.0.3", {"start": v(87.12, 11.82) * mm, "end": v(89.36, 11.82) * mm});
            skLineSegment(sketch, "E14.35.0.0", {"start": v(90.53, 7.25) * mm, "end": v(92.76, 7.25) * mm});
            skLineSegment(sketch, "E14.35.0.1", {"start": v(96.16, 11.82) * mm, "end": v(97.33, 7.25) * mm});
            skLineSegment(sketch, "E14.35.0.2", {"start": v(93.93, 11.82) * mm, "end": v(92.76, 7.25) * mm});
            skLineSegment(sketch, "E14.35.0.3", {"start": v(93.93, 11.82) * mm, "end": v(96.16, 11.82) * mm});
            skLineSegment(sketch, "E14.36.0.0", {"start": v(97.33, 7.25) * mm, "end": v(99.57, 7.25) * mm});
            skLineSegment(sketch, "E14.36.0.1", {"start": v(102.97, 11.82) * mm, "end": v(104.14, 7.25) * mm});
            skLineSegment(sketch, "E14.36.0.2", {"start": v(100.74, 11.82) * mm, "end": v(99.57, 7.25) * mm});
            skLineSegment(sketch, "E14.36.0.3", {"start": v(100.74, 11.82) * mm, "end": v(102.97, 11.82) * mm});
            skLineSegment(sketch, "E14.37.0.0", {"start": v(104.14, 7.25) * mm, "end": v(106.38, 7.25) * mm});
            skLineSegment(sketch, "E14.37.0.1", {"start": v(109.78, 11.82) * mm, "end": v(110.95, 7.25) * mm});
            skLineSegment(sketch, "E14.37.0.2", {"start": v(107.54, 11.82) * mm, "end": v(106.38, 7.25) * mm});
            skLineSegment(sketch, "E14.37.0.3", {"start": v(107.54, 11.82) * mm, "end": v(109.78, 11.82) * mm});
            skLineSegment(sketch, "E14.38.0.0", {"start": v(110.95, 7.25) * mm, "end": v(113.18, 7.25) * mm});
            skLineSegment(sketch, "E14.38.0.1", {"start": v(116.59, 11.82) * mm, "end": v(117.75, 7.25) * mm});
            skLineSegment(sketch, "E14.38.0.2", {"start": v(114.35, 11.82) * mm, "end": v(113.18, 7.25) * mm});
            skLineSegment(sketch, "E14.38.0.3", {"start": v(114.35, 11.82) * mm, "end": v(116.59, 11.82) * mm});
            skLineSegment(sketch, "E14.39.0.0", {"start": v(117.75, 7.25) * mm, "end": v(119.99, 7.25) * mm});
            skLineSegment(sketch, "E14.39.0.1", {"start": v(123.4, 11.82) * mm, "end": v(124.56, 7.25) * mm});
            skLineSegment(sketch, "E14.39.0.2", {"start": v(121.16, 11.82) * mm, "end": v(119.99, 7.25) * mm});
            skLineSegment(sketch, "E14.39.0.3", {"start": v(121.16, 11.82) * mm, "end": v(123.4, 11.82) * mm});
            skLineSegment(sketch, "E14.40.0.0", {"start": v(124.56, 7.25) * mm, "end": v(126.8, 7.25) * mm});
            skLineSegment(sketch, "E14.40.0.1", {"start": v(130.2, 11.82) * mm, "end": v(131.37, 7.25) * mm});
            skLineSegment(sketch, "E14.40.0.2", {"start": v(127.97, 11.82) * mm, "end": v(126.8, 7.25) * mm});
            skLineSegment(sketch, "E14.40.0.3", {"start": v(127.97, 11.82) * mm, "end": v(130.2, 11.82) * mm});
            skLineSegment(sketch, "E14.41.0.0", {"start": v(131.37, 7.25) * mm, "end": v(133.6, 7.25) * mm});
            skLineSegment(sketch, "E14.41.0.1", {"start": v(137, 11.82) * mm, "end": v(138.18, 7.25) * mm});
            skLineSegment(sketch, "E14.41.0.2", {"start": v(134.77, 11.82) * mm, "end": v(133.6, 7.25) * mm});
            skLineSegment(sketch, "E14.41.0.3", {"start": v(134.77, 11.82) * mm, "end": v(137, 11.82) * mm});
            skLineSegment(sketch, "E14.42.0.0", {"start": v(138.18, 7.25) * mm, "end": v(140.41, 7.25) * mm});
            skLineSegment(sketch, "E14.42.0.1", {"start": v(143.81, 11.82) * mm, "end": v(144.98, 7.25) * mm});
            skLineSegment(sketch, "E14.42.0.2", {"start": v(141.58, 11.82) * mm, "end": v(140.41, 7.25) * mm});
            skLineSegment(sketch, "E14.42.0.3", {"start": v(141.58, 11.82) * mm, "end": v(143.81, 11.82) * mm});
            skLineSegment(sketch, "E14.43.0.0", {"start": v(144.98, 7.25) * mm, "end": v(147.22, 7.25) * mm});
            skLineSegment(sketch, "E14.43.0.1", {"start": v(150.62, 11.82) * mm, "end": v(151.8, 7.25) * mm});
            skLineSegment(sketch, "E14.43.0.2", {"start": v(148.39, 11.82) * mm, "end": v(147.22, 7.25) * mm});
            skLineSegment(sketch, "E14.43.0.3", {"start": v(148.39, 11.82) * mm, "end": v(150.62, 11.82) * mm});
            skLineSegment(sketch, "E14.44.0.0", {"start": v(151.8, 7.25) * mm, "end": v(154.03, 7.25) * mm});
            skLineSegment(sketch, "E14.44.0.1", {"start": v(157.43, 11.82) * mm, "end": v(158.6, 7.25) * mm});
            skLineSegment(sketch, "E14.44.0.2", {"start": v(155.2, 11.82) * mm, "end": v(154.03, 7.25) * mm});
            skLineSegment(sketch, "E14.44.0.3", {"start": v(155.2, 11.82) * mm, "end": v(157.43, 11.82) * mm});
            skLineSegment(sketch, "E14.45.0.0", {"start": v(158.6, 7.25) * mm, "end": v(160.83, 7.25) * mm});
            skLineSegment(sketch, "E14.45.0.1", {"start": v(164.24, 11.82) * mm, "end": v(165.4, 7.25) * mm});
            skLineSegment(sketch, "E14.45.0.2", {"start": v(162, 11.82) * mm, "end": v(160.83, 7.25) * mm});
            skLineSegment(sketch, "E14.45.0.3", {"start": v(162, 11.82) * mm, "end": v(164.24, 11.82) * mm});
            skLineSegment(sketch, "E14.46.0.0", {"start": v(165.4, 7.25) * mm, "end": v(167.64, 7.25) * mm});
            skLineSegment(sketch, "E14.46.0.1", {"start": v(171.04, 11.82) * mm, "end": v(172.21, 7.25) * mm});
            skLineSegment(sketch, "E14.46.0.2", {"start": v(168.8, 11.82) * mm, "end": v(167.64, 7.25) * mm});
            skLineSegment(sketch, "E14.46.0.3", {"start": v(168.8, 11.82) * mm, "end": v(171.04, 11.82) * mm});
            skLineSegment(sketch, "E14.47.0.0", {"start": v(172.21, 7.25) * mm, "end": v(174.45, 7.25) * mm});
            skLineSegment(sketch, "E14.47.0.1", {"start": v(177.85, 11.82) * mm, "end": v(179.02, 7.25) * mm});
            skLineSegment(sketch, "E14.47.0.2", {"start": v(175.62, 11.82) * mm, "end": v(174.45, 7.25) * mm});
            skLineSegment(sketch, "E14.47.0.3", {"start": v(175.62, 11.82) * mm, "end": v(177.85, 11.82) * mm});
            skLineSegment(sketch, "E14.48.0.0", {"start": v(179.02, 7.25) * mm, "end": v(181.25, 7.25) * mm});
            skLineSegment(sketch, "E14.48.0.1", {"start": v(184.66, 11.82) * mm, "end": v(185.83, 7.25) * mm});
            skLineSegment(sketch, "E14.48.0.2", {"start": v(182.42, 11.82) * mm, "end": v(181.25, 7.25) * mm});
            skLineSegment(sketch, "E14.48.0.3", {"start": v(182.42, 11.82) * mm, "end": v(184.66, 11.82) * mm});
            skLineSegment(sketch, "E14.49.0.0", {"start": v(185.83, 7.25) * mm, "end": v(188.06, 7.25) * mm});
            skLineSegment(sketch, "E14.49.0.1", {"start": v(191.47, 11.82) * mm, "end": v(192.63, 7.25) * mm});
            skLineSegment(sketch, "E14.49.0.2", {"start": v(189.23, 11.82) * mm, "end": v(188.06, 7.25) * mm});
            skLineSegment(sketch, "E14.49.0.3", {"start": v(189.23, 11.82) * mm, "end": v(191.47, 11.82) * mm});
            skLineSegment(sketch, "E14.direction1", {"start": v(-147.73, 7.25) * mm, "end": v(-140.92, 7.25) * mm, "construction": true});
            skLineSegment(sketch, "E15.1.0.0", {"start": v(192.63, 7.25) * mm, "end": v(194.87, 7.25) * mm});
            skLineSegment(sketch, "E15.1.0.1", {"start": v(198.27, 11.82) * mm, "end": v(199.44, 7.25) * mm});
            skLineSegment(sketch, "E15.1.0.2", {"start": v(196.04, 11.82) * mm, "end": v(194.87, 7.25) * mm});
            skLineSegment(sketch, "E15.1.0.3", {"start": v(196.04, 11.82) * mm, "end": v(198.27, 11.82) * mm});
            skLineSegment(sketch, "E15.2.0.0", {"start": v(199.44, 7.25) * mm, "end": v(201.68, 7.25) * mm});
            skLineSegment(sketch, "E15.2.0.1", {"start": v(205.08, 11.82) * mm, "end": v(206.25, 7.25) * mm});
            skLineSegment(sketch, "E15.2.0.2", {"start": v(202.84, 11.82) * mm, "end": v(201.68, 7.25) * mm});
            skLineSegment(sketch, "E15.2.0.3", {"start": v(202.84, 11.82) * mm, "end": v(205.08, 11.82) * mm});
            skLineSegment(sketch, "E15.3.0.0", {"start": v(206.25, 7.25) * mm, "end": v(208.48, 7.25) * mm});
            skLineSegment(sketch, "E15.3.0.1", {"start": v(211.89, 11.82) * mm, "end": v(213.06, 7.25) * mm});
            skLineSegment(sketch, "E15.3.0.2", {"start": v(209.65, 11.82) * mm, "end": v(208.48, 7.25) * mm});
            skLineSegment(sketch, "E15.3.0.3", {"start": v(209.65, 11.82) * mm, "end": v(211.89, 11.82) * mm});
            skLineSegment(sketch, "E15.4.0.0", {"start": v(213.06, 7.25) * mm, "end": v(215.3, 7.25) * mm});
            skLineSegment(sketch, "E15.4.0.1", {"start": v(218.7, 11.82) * mm, "end": v(219.86, 7.25) * mm});
            skLineSegment(sketch, "E15.4.0.2", {"start": v(216.46, 11.82) * mm, "end": v(215.3, 7.25) * mm});
            skLineSegment(sketch, "E15.4.0.3", {"start": v(216.46, 11.82) * mm, "end": v(218.7, 11.82) * mm});
            skLineSegment(sketch, "E15.5.0.0", {"start": v(219.86, 7.25) * mm, "end": v(222.1, 7.25) * mm});
            skLineSegment(sketch, "E15.5.0.1", {"start": v(225.5, 11.82) * mm, "end": v(226.67, 7.25) * mm});
            skLineSegment(sketch, "E15.5.0.2", {"start": v(223.27, 11.82) * mm, "end": v(222.1, 7.25) * mm});
            skLineSegment(sketch, "E15.5.0.3", {"start": v(223.27, 11.82) * mm, "end": v(225.5, 11.82) * mm});
            skLineSegment(sketch, "E15.6.0.0", {"start": v(226.67, 7.25) * mm, "end": v(228.9, 7.25) * mm});
            skLineSegment(sketch, "E15.6.0.1", {"start": v(232.3, 11.82) * mm, "end": v(233.48, 7.25) * mm});
            skLineSegment(sketch, "E15.6.0.2", {"start": v(230.07, 11.82) * mm, "end": v(228.9, 7.25) * mm});
            skLineSegment(sketch, "E15.6.0.3", {"start": v(230.07, 11.82) * mm, "end": v(232.3, 11.82) * mm});
            skLineSegment(sketch, "E15.7.0.0", {"start": v(233.48, 7.25) * mm, "end": v(235.71, 7.25) * mm});
            skLineSegment(sketch, "E15.7.0.1", {"start": v(239.12, 11.82) * mm, "end": v(240.28, 7.25) * mm});
            skLineSegment(sketch, "E15.7.0.2", {"start": v(236.88, 11.82) * mm, "end": v(235.71, 7.25) * mm});
            skLineSegment(sketch, "E15.7.0.3", {"start": v(236.88, 11.82) * mm, "end": v(239.12, 11.82) * mm});
            skLineSegment(sketch, "E15.8.0.0", {"start": v(240.28, 7.25) * mm, "end": v(242.52, 7.25) * mm});
            skLineSegment(sketch, "E15.8.0.1", {"start": v(245.92, 11.82) * mm, "end": v(247.1, 7.25) * mm});
            skLineSegment(sketch, "E15.8.0.2", {"start": v(243.69, 11.82) * mm, "end": v(242.52, 7.25) * mm});
            skLineSegment(sketch, "E15.8.0.3", {"start": v(243.69, 11.82) * mm, "end": v(245.92, 11.82) * mm});
            skLineSegment(sketch, "E15.9.0.0", {"start": v(247.1, 7.25) * mm, "end": v(249.33, 7.25) * mm});
            skLineSegment(sketch, "E15.9.0.1", {"start": v(252.73, 11.82) * mm, "end": v(253.9, 7.25) * mm});
            skLineSegment(sketch, "E15.9.0.2", {"start": v(250.5, 11.82) * mm, "end": v(249.33, 7.25) * mm});
            skLineSegment(sketch, "E15.9.0.3", {"start": v(250.5, 11.82) * mm, "end": v(252.73, 11.82) * mm});
            skLineSegment(sketch, "E15.10.0.0", {"start": v(253.9, 7.25) * mm, "end": v(256.13, 7.25) * mm});
            skLineSegment(sketch, "E15.10.0.1", {"start": v(259.54, 11.82) * mm, "end": v(260.7, 7.25) * mm});
            skLineSegment(sketch, "E15.10.0.2", {"start": v(257.3, 11.82) * mm, "end": v(256.13, 7.25) * mm});
            skLineSegment(sketch, "E15.10.0.3", {"start": v(257.3, 11.82) * mm, "end": v(259.54, 11.82) * mm});
            skLineSegment(sketch, "E15.11.0.0", {"start": v(260.7, 7.25) * mm, "end": v(262.94, 7.25) * mm});
            skLineSegment(sketch, "E15.11.0.1", {"start": v(266.34, 11.82) * mm, "end": v(267.51, 7.25) * mm});
            skLineSegment(sketch, "E15.11.0.2", {"start": v(264.1, 11.82) * mm, "end": v(262.94, 7.25) * mm});
            skLineSegment(sketch, "E15.11.0.3", {"start": v(264.1, 11.82) * mm, "end": v(266.34, 11.82) * mm});
            skLineSegment(sketch, "E15.12.0.0", {"start": v(267.51, 7.25) * mm, "end": v(269.75, 7.25) * mm});
            skLineSegment(sketch, "E15.12.0.1", {"start": v(273.15, 11.82) * mm, "end": v(274.32, 7.25) * mm});
            skLineSegment(sketch, "E15.12.0.2", {"start": v(270.92, 11.82) * mm, "end": v(269.75, 7.25) * mm});
            skLineSegment(sketch, "E15.12.0.3", {"start": v(270.92, 11.82) * mm, "end": v(273.15, 11.82) * mm});
            skLineSegment(sketch, "E15.13.0.0", {"start": v(274.32, 7.25) * mm, "end": v(276.56, 7.25) * mm});
            skLineSegment(sketch, "E15.13.0.1", {"start": v(279.96, 11.82) * mm, "end": v(281.13, 7.25) * mm});
            skLineSegment(sketch, "E15.13.0.2", {"start": v(277.72, 11.82) * mm, "end": v(276.56, 7.25) * mm});
            skLineSegment(sketch, "E15.13.0.3", {"start": v(277.72, 11.82) * mm, "end": v(279.96, 11.82) * mm});
            skLineSegment(sketch, "E15.14.0.0", {"start": v(281.13, 7.25) * mm, "end": v(283.36, 7.25) * mm});
            skLineSegment(sketch, "E15.14.0.1", {"start": v(286.77, 11.82) * mm, "end": v(287.93, 7.25) * mm});
            skLineSegment(sketch, "E15.14.0.2", {"start": v(284.53, 11.82) * mm, "end": v(283.36, 7.25) * mm});
            skLineSegment(sketch, "E15.14.0.3", {"start": v(284.53, 11.82) * mm, "end": v(286.77, 11.82) * mm});
            skLineSegment(sketch, "E15.15.0.0", {"start": v(287.93, 7.25) * mm, "end": v(290.17, 7.25) * mm});
            skLineSegment(sketch, "E15.15.0.1", {"start": v(293.57, 11.82) * mm, "end": v(294.74, 7.25) * mm});
            skLineSegment(sketch, "E15.15.0.2", {"start": v(291.34, 11.82) * mm, "end": v(290.17, 7.25) * mm});
            skLineSegment(sketch, "E15.15.0.3", {"start": v(291.34, 11.82) * mm, "end": v(293.57, 11.82) * mm});
            skLineSegment(sketch, "E15.16.0.0", {"start": v(294.74, 7.25) * mm, "end": v(296.98, 7.25) * mm});
            skLineSegment(sketch, "E15.16.0.1", {"start": v(300.38, 11.82) * mm, "end": v(301.55, 7.25) * mm});
            skLineSegment(sketch, "E15.16.0.2", {"start": v(298.15, 11.82) * mm, "end": v(296.98, 7.25) * mm});
            skLineSegment(sketch, "E15.16.0.3", {"start": v(298.15, 11.82) * mm, "end": v(300.38, 11.82) * mm});
            skLineSegment(sketch, "E15.17.0.0", {"start": v(301.55, 7.25) * mm, "end": v(303.78, 7.25) * mm});
            skLineSegment(sketch, "E15.17.0.1", {"start": v(307.19, 11.82) * mm, "end": v(308.36, 7.25) * mm});
            skLineSegment(sketch, "E15.17.0.2", {"start": v(304.95, 11.82) * mm, "end": v(303.78, 7.25) * mm});
            skLineSegment(sketch, "E15.17.0.3", {"start": v(304.95, 11.82) * mm, "end": v(307.19, 11.82) * mm});
            skLineSegment(sketch, "E15.18.0.0", {"start": v(308.36, 7.25) * mm, "end": v(310.6, 7.25) * mm});
            skLineSegment(sketch, "E15.18.0.1", {"start": v(314, 11.82) * mm, "end": v(315.16, 7.25) * mm});
            skLineSegment(sketch, "E15.18.0.2", {"start": v(311.76, 11.82) * mm, "end": v(310.6, 7.25) * mm});
            skLineSegment(sketch, "E15.18.0.3", {"start": v(311.76, 11.82) * mm, "end": v(314, 11.82) * mm});
            skLineSegment(sketch, "E15.19.0.0", {"start": v(315.16, 7.25) * mm, "end": v(317.4, 7.25) * mm});
            skLineSegment(sketch, "E15.19.0.1", {"start": v(320.8, 11.82) * mm, "end": v(321.97, 7.25) * mm});
            skLineSegment(sketch, "E15.19.0.2", {"start": v(318.57, 11.82) * mm, "end": v(317.4, 7.25) * mm});
            skLineSegment(sketch, "E15.19.0.3", {"start": v(318.57, 11.82) * mm, "end": v(320.8, 11.82) * mm});
            skLineSegment(sketch, "E15.20.0.0", {"start": v(321.97, 7.25) * mm, "end": v(324.2, 7.25) * mm});
            skLineSegment(sketch, "E15.20.0.1", {"start": v(327.6, 11.82) * mm, "end": v(328.78, 7.25) * mm});
            skLineSegment(sketch, "E15.20.0.2", {"start": v(325.37, 11.82) * mm, "end": v(324.2, 7.25) * mm});
            skLineSegment(sketch, "E15.20.0.3", {"start": v(325.37, 11.82) * mm, "end": v(327.6, 11.82) * mm});
            skLineSegment(sketch, "E15.21.0.0", {"start": v(328.78, 7.25) * mm, "end": v(331.01, 7.25) * mm});
            skLineSegment(sketch, "E15.21.0.1", {"start": v(334.42, 11.82) * mm, "end": v(335.58, 7.25) * mm});
            skLineSegment(sketch, "E15.21.0.2", {"start": v(332.18, 11.82) * mm, "end": v(331.01, 7.25) * mm});
            skLineSegment(sketch, "E15.21.0.3", {"start": v(332.18, 11.82) * mm, "end": v(334.42, 11.82) * mm});
            skLineSegment(sketch, "E15.22.0.0", {"start": v(335.58, 7.25) * mm, "end": v(337.82, 7.25) * mm});
            skLineSegment(sketch, "E15.22.0.1", {"start": v(341.22, 11.82) * mm, "end": v(342.4, 7.25) * mm});
            skLineSegment(sketch, "E15.22.0.2", {"start": v(338.99, 11.82) * mm, "end": v(337.82, 7.25) * mm});
            skLineSegment(sketch, "E15.22.0.3", {"start": v(338.99, 11.82) * mm, "end": v(341.22, 11.82) * mm});
            skLineSegment(sketch, "E15.23.0.0", {"start": v(342.4, 7.25) * mm, "end": v(344.63, 7.25) * mm});
            skLineSegment(sketch, "E15.23.0.1", {"start": v(348.03, 11.82) * mm, "end": v(349.2, 7.25) * mm});
            skLineSegment(sketch, "E15.23.0.2", {"start": v(345.8, 11.82) * mm, "end": v(344.63, 7.25) * mm});
            skLineSegment(sketch, "E15.23.0.3", {"start": v(345.8, 11.82) * mm, "end": v(348.03, 11.82) * mm});
            skLineSegment(sketch, "E15.24.0.0", {"start": v(349.2, 7.25) * mm, "end": v(351.43, 7.25) * mm});
            skLineSegment(sketch, "E15.24.0.1", {"start": v(354.84, 11.82) * mm, "end": v(356, 7.25) * mm});
            skLineSegment(sketch, "E15.24.0.2", {"start": v(352.6, 11.82) * mm, "end": v(351.43, 7.25) * mm});
            skLineSegment(sketch, "E15.24.0.3", {"start": v(352.6, 11.82) * mm, "end": v(354.84, 11.82) * mm});
            skLineSegment(sketch, "E15.25.0.0", {"start": v(356, 7.25) * mm, "end": v(358.24, 7.25) * mm});
            skLineSegment(sketch, "E15.25.0.1", {"start": v(361.65, 11.82) * mm, "end": v(362.81, 7.25) * mm});
            skLineSegment(sketch, "E15.25.0.2", {"start": v(359.41, 11.82) * mm, "end": v(358.24, 7.25) * mm});
            skLineSegment(sketch, "E15.25.0.3", {"start": v(359.41, 11.82) * mm, "end": v(361.65, 11.82) * mm});
            skLineSegment(sketch, "E15.26.0.0", {"start": v(362.81, 7.25) * mm, "end": v(365.05, 7.25) * mm});
            skLineSegment(sketch, "E15.26.0.1", {"start": v(368.45, 11.82) * mm, "end": v(369.62, 7.25) * mm});
            skLineSegment(sketch, "E15.26.0.2", {"start": v(366.22, 11.82) * mm, "end": v(365.05, 7.25) * mm});
            skLineSegment(sketch, "E15.26.0.3", {"start": v(366.22, 11.82) * mm, "end": v(368.45, 11.82) * mm});
            skLineSegment(sketch, "E15.27.0.0", {"start": v(369.62, 7.25) * mm, "end": v(371.86, 7.25) * mm});
            skLineSegment(sketch, "E15.27.0.1", {"start": v(375.26, 11.82) * mm, "end": v(376.43, 7.25) * mm});
            skLineSegment(sketch, "E15.27.0.2", {"start": v(373.02, 11.82) * mm, "end": v(371.86, 7.25) * mm});
            skLineSegment(sketch, "E15.27.0.3", {"start": v(373.02, 11.82) * mm, "end": v(375.26, 11.82) * mm});
            skLineSegment(sketch, "E15.28.0.0", {"start": v(376.43, 7.25) * mm, "end": v(378.66, 7.25) * mm});
            skLineSegment(sketch, "E15.28.0.1", {"start": v(382.07, 11.82) * mm, "end": v(383.24, 7.25) * mm});
            skLineSegment(sketch, "E15.28.0.2", {"start": v(379.83, 11.82) * mm, "end": v(378.66, 7.25) * mm});
            skLineSegment(sketch, "E15.28.0.3", {"start": v(379.83, 11.82) * mm, "end": v(382.07, 11.82) * mm});
            skLineSegment(sketch, "E15.29.0.0", {"start": v(383.24, 7.25) * mm, "end": v(385.47, 7.25) * mm});
            skLineSegment(sketch, "E15.29.0.1", {"start": v(388.87, 11.82) * mm, "end": v(390.04, 7.25) * mm});
            skLineSegment(sketch, "E15.29.0.2", {"start": v(386.64, 11.82) * mm, "end": v(385.47, 7.25) * mm});
            skLineSegment(sketch, "E15.29.0.3", {"start": v(386.64, 11.82) * mm, "end": v(388.87, 11.82) * mm});
            skLineSegment(sketch, "E15.30.0.0", {"start": v(390.04, 7.25) * mm, "end": v(392.28, 7.25) * mm});
            skLineSegment(sketch, "E15.30.0.1", {"start": v(395.68, 11.82) * mm, "end": v(396.85, 7.25) * mm});
            skLineSegment(sketch, "E15.30.0.2", {"start": v(393.45, 11.82) * mm, "end": v(392.28, 7.25) * mm});
            skLineSegment(sketch, "E15.30.0.3", {"start": v(393.45, 11.82) * mm, "end": v(395.68, 11.82) * mm});
            skLineSegment(sketch, "E15.31.0.0", {"start": v(396.85, 7.25) * mm, "end": v(399.08, 7.25) * mm});
            skLineSegment(sketch, "E15.31.0.1", {"start": v(402.49, 11.82) * mm, "end": v(403.66, 7.25) * mm});
            skLineSegment(sketch, "E15.31.0.2", {"start": v(400.25, 11.82) * mm, "end": v(399.08, 7.25) * mm});
            skLineSegment(sketch, "E15.31.0.3", {"start": v(400.25, 11.82) * mm, "end": v(402.49, 11.82) * mm});
            skLineSegment(sketch, "E15.32.0.0", {"start": v(403.66, 7.25) * mm, "end": v(405.9, 7.25) * mm});
            skLineSegment(sketch, "E15.direction1", {"start": v(185.83, 7.25) * mm, "end": v(192.63, 7.25) * mm, "construction": true});
            skSolve(sketch);
        }
        {
            var Q0;
            Q0=qSketchRegion(id+"F2",true);
            extrude(context, id + "F3", {"entities" : qUnion([Q0]), "operationType" : NewBodyOperationType.ADD, "oppositeDirection" : true, "depth" : 19.05 * mm});
        }
        {
            var Q0;
            Q0=makeQuery(id+"F1.opExtrude","SWEPT_FACE",FACE,{"disambiguationData":[OSD([sQuery(id+"F0.wireOp",EDGE,"E0.top")])]});
            var sketch = newSketch(context, id + "F4", { "sketchPlane" : qUnion([Q0])});
            skLineSegment(sketch, "E16.0", {"start": v(-406.4, 9.53) * mm, "end": v(-406.4, -9.52) * mm, "construction": true});
            skLineSegment(sketch, "E17.0", {"start": v(-342.9, 9.53) * mm, "end": v(-342.9, -9.52) * mm, "construction": true});
            skPoint(sketch, "E18", {"position": v(-342.9, 0) * mm});
            skPoint(sketch, "E19.1.0.0", {"position": v(-114.3, 0) * mm});
            skPoint(sketch, "E19.2.0.0", {"position": v(114.3, 0) * mm});
            skPoint(sketch, "E19.3.0.0", {"position": v(342.9, 0) * mm});
            skLineSegment(sketch, "E19.direction1", {"start": v(-342.9, 0) * mm, "end": v(-114.3, 0) * mm, "construction": true});
            skSolve(sketch);
        }
        {
            var Q0;
            Q0=sQuery(id+"F4.wireOp",VERTEX,"E18");
            var Q1;
            Q1=sQuery(id+"F4.wireOp",VERTEX,"E19.1.0.0");
            var Q2;
            Q2=sQuery(id+"F4.wireOp",VERTEX,"E19.2.0.0");
            var Q3;
            Q3=sQuery(id+"F4.wireOp",VERTEX,"E19.3.0.0");
            var Q4;
            Q4=makeQuery(id+"F1.opExtrude","SWEPT_BODY",BODY,{"disambiguationData":[OSD([sQuery(id+"F0.wireOp",EDGE,"E0.bottom"),sQuery(id+"F0.wireOp",EDGE,"E0.top"),sQuery(id+"F0.wireOp",EDGE,"E0.left"),sQuery(id+"F0.wireOp",EDGE,"E0.right")])]});
            hole(context, id + "F5", {"style" : HoleStyle.SIMPLE, "endStyle" : HoleEndStyle.THROUGH, "standardTappedOrClearance" : lookupTablePath({ "standard" : "ANSI", "engagement" : "75%", "pitch" : "16 tpi", "size" : "3/8", "type" : "Tapped" }), "standardBlindInLast" : lookupTablePath({ "standard" : "ANSI", "engagement" : "75%", "pitch" : "16 tpi", "size" : "3/8", "type" : "Tapped" }), "holeDiameter" : 7.94 * mm, "locations" : qUnion([Q0, Q1, Q2, Q3]), "scope" : qUnion([Q4]), "isTappedThrough" : true, "majorDiameter" : 9.53 * mm, "showTappedDepth" : true});
        }
    });
